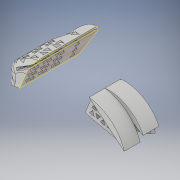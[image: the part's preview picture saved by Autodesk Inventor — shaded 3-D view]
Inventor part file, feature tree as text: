
AUTODESK INVENTOR PART (.ipt)
format: ipt  version: 2017 (Build 210142000, 142)  size: 1,422,336 bytes
history: native  units: mm
features: sketch x29, extrude x25, plane x7, fillet x6, other x4, move_body x2, boolean_combine x1, revolve x1, sweep x1, split x1
ambient origin geometry x8: Origin, YZ Plane, XZ Plane, XY Plane, X Axis, Y Axis, Z Axis, Center Point
bodies: Solid1 (feature_tree), Solid2 (feature_tree), Solid3 (feature_tree), Solid4 (feature_tree), Solid5 (feature_tree), Solid6 (feature_tree), Solid7 (feature_tree)
feature tree (77):
  extrude  "Extrusion1"  Depth=35.0mm
  plane  "Work Plane1"
  extrude  "Extrusion2"  Depth=33.005mm
  extrude  "Extrusion3"  TaperAngle=0.0deg  [1 undecoded]
  plane  "Work Plane2"
  extrude  "Extrusion4"  Depth=20.0mm
  other  "Work Axis1"
  extrude  "Extrusion5"  Depth=10.0mm
  sketch  "Sketch6"  dims[d12=48.556624mm d13=20.0mm d14=0.0mm]
  boolean_combine  "Combine1"
  extrude  "Extrusion6"  Depth=20.0mm TaperAngle=0.0deg
  extrude  "Extrusion7"  Depth=20.0mm TaperAngle=0.0deg
  other  "Work Axis2"
  fillet  "Fillet1"  Radius=53.287466mm
  revolve  "Revolution1"  [1 undecoded]
  extrude  "Extrusion8"  Depth=61.358233mm
  sketch  "Sketch10"  dims[d25=7.433428mm d26=13.25mm d27=0.0mm]
  plane  "Work Plane3"
  sweep  "Sweep1"
  extrude  "Extrusion9"  TaperAngle=90.0deg  [1 undecoded]
  fillet  "Fillet2"  Radius=40.197898mm
  extrude  "Extrusion10"  Depth=15.060899mm
  extrude  "Extrusion11"  Depth=10.650813mm
  extrude  "Extrusion12"  Depth=5.3475mm
  fillet  "Fillet3"  Radius=15.0mm
  fillet  "Fillet4"  [1 undecoded]
  fillet  "Fillet5"  Radius=27.295196mm
  other  "Bend Part1"
  extrude  "Extrusion13"  Depth=5.348mm
  plane  "Work Plane4"
  extrude  "Extrusion14"  TaperAngle=0.0deg  [1 undecoded]
  fillet  "Fillet6"  Radius=13.25mm
  extrude  "Extrusion15"  Depth=10.0mm TaperAngle=0.0deg
  plane  "Work Plane5"
  extrude  "Extrusion16"  Depth=10.0mm
  extrude  "Extrusion22"  Depth=10.0mm TaperAngle=0.0deg
  extrude  "Extrusion23"  Depth=10.0mm
  extrude  "Extrusion24"  Depth=10.0mm TaperAngle=180.0deg
  extrude  "Extrusion25"  Depth=18.153275mm
  plane  "Work Plane7"
  extrude  "Extrusion26"  TaperAngle=90.0deg  [1 undecoded]
  extrude  "Extrusion27"  Depth=57.396209mm
  extrude  "Extrusion28"  Depth=2.0mm
  plane  "Work Plane8"
  extrude  "Extrusion29"  Depth=17.5mm
  split  "Split1"
  move_body  "Move Body1"
  move_body  "Move Body2"
  sketch  "Sketch1"  dims[d0=60.0mm d1=35.0mm]
  sketch  "Sketch2"  dims[d2=60.0mm d3=33.005mm]
  sketch  "Sketch3"  dims[d4=75.0mm d5=0.0mm d6=0.0mm]
  sketch  "Sketch4"  dims[d7=35.0mm d8=20.0mm]
  sketch  "Sketch5"  dims[d9=55.0mm d10=0.0mm d11=10.0mm]
  sketch  "Sketch7"  dims[d15=90.0deg d16=20.0mm d17=0.0mm d18=53.287466mm]
  sketch  "Sketch8"  dims[d19=20.0mm d20=0.0mm d21=14.476257mm]
  sketch  "Sketch9"  dims[d22=20.0mm d23=0.0mm d24=61.358233mm]
  sketch  "Sketch11"  dims[d28=10.0mm d29=90.0deg d30=40.197898mm]
  sketch  "Sketch12"  dims[d31=90.965929mm d32=15.060899mm]
  sketch  "Sketch13"  dims[d33=0.0mm d34=0.0mm d35=10.650813mm]
  sketch  "Sketch15"  dims[d36=90.0deg d37=5.3475mm d38=15.0mm d39=45.0deg d40=27.295196mm]
  sketch  "Sketch16"  dims[d41=20.0mm d42=5.348mm]
  sketch  "Sketch18"  dims[d43=60.0mm d44=0.0mm d45=0.0mm d46=13.25mm d47=0.0mm]
  sketch  "Sketch19"  dims[d48=10.0mm d49=75.0mm d50=0.0mm]
  sketch  "Sketch20"  dims[d52=10.0mm d53=10.80569mm]
  sketch  "Sketch21"  dims[d54=10.0mm d55=0.0mm d56=4.8mm d57=0.0mm]
  sketch  "Sketch22"  dims[d58=10.0mm d59=10.0mm]
  sketch  "Sketch28"  dims[d60=10.0mm d62=2.0mm d63=180.0deg]
  sketch  "Sketch29"  dims[d64=18.153275mm d65=18.153275mm]
  sketch  "Sketch30"  dims[d66=75.0mm d67=0.0mm d68=90.0deg]
  sketch  "Sketch31"  dims[d69=75.0mm d70=57.396209mm]
  sketch  "Sketch32"  dims[d71=75.0mm d72=0.0mm d73=2.0mm]
  sketch  "Sketch33"  dims[d74=27.7545mm d75=17.5mm]
  sketch  "Sketch34"  dims[d76=5.0mm d77=0.0mm d78=20.0mm]
  sketch  "Sketch35"  dims[d79=28.8585mm]
  sketch  "Sketch36"  dims[d80=10.0mm d81=0.0mm d108=10.0mm d109=0.0mm d110=5.0mm d111=0.0mm d112=20.0mm d113=3.0mm d114=2.5mm d115=19.198622mm d116=10.0mm d117=0.0mm d118=20.0mm d119=3.0mm d120=13.189mm d121=20.0mm d122=3.0mm d123=11.073mm d124=10.0mm d125=5.0mm d126=0.0mm d127=0.0mm d128=5.202827mm d129=2.5mm d130=20.0mm d131=47.662mm d132=0.0mm d133=6.0mm d134=4.0mm d136=4.0mm d137=6.0mm d138=4.0mm d140=4.0mm d141=30.0mm d143=16.0mm d144=30.0mm d146=8.0mm d149=20.0mm d151=19.0mm d152=10.0mm d154=10.0mm d156=20.0mm d158=8.0mm d159=10.0mm d161=10.0mm d163=0.0mm d164=0.0mm d165=6.0mm d166=4.0mm d167=4.0mm d168=6.0mm d169=4.0mm d170=4.0mm d171=20.0mm d173=14.0mm d174=20.0mm d176=8.0mm d179=10.0mm d180=0.0mm d181=10.0mm d182=6.0mm d183=4.0mm d185=4.0mm d186=6.0mm d187=4.0mm d188=4.0mm d189=40.0mm d191=14.0mm d192=10.0mm d194=10.0mm d196=20.0mm d198=12.0mm d199=10.0mm d201=10.0mm d203=20.0mm d205=8.0mm d206=10.0mm d208=10.0mm d210=20.0mm d211=0.0mm d213=10.0mm d214=0.0mm d215=10.0mm d216=0.0mm d217=0.0mm d218=34.0mm d219=-28.75mm d220=14.5mm]
  other  "Srf1"
  extrude  "ExtrusionSrf1"  Depth=20.0mm
note: 6 required parameter values undecoded (feature->parameter linkage not recoverable at this tier; creation-order binding heuristic only, values carry confidence <= 0.55)